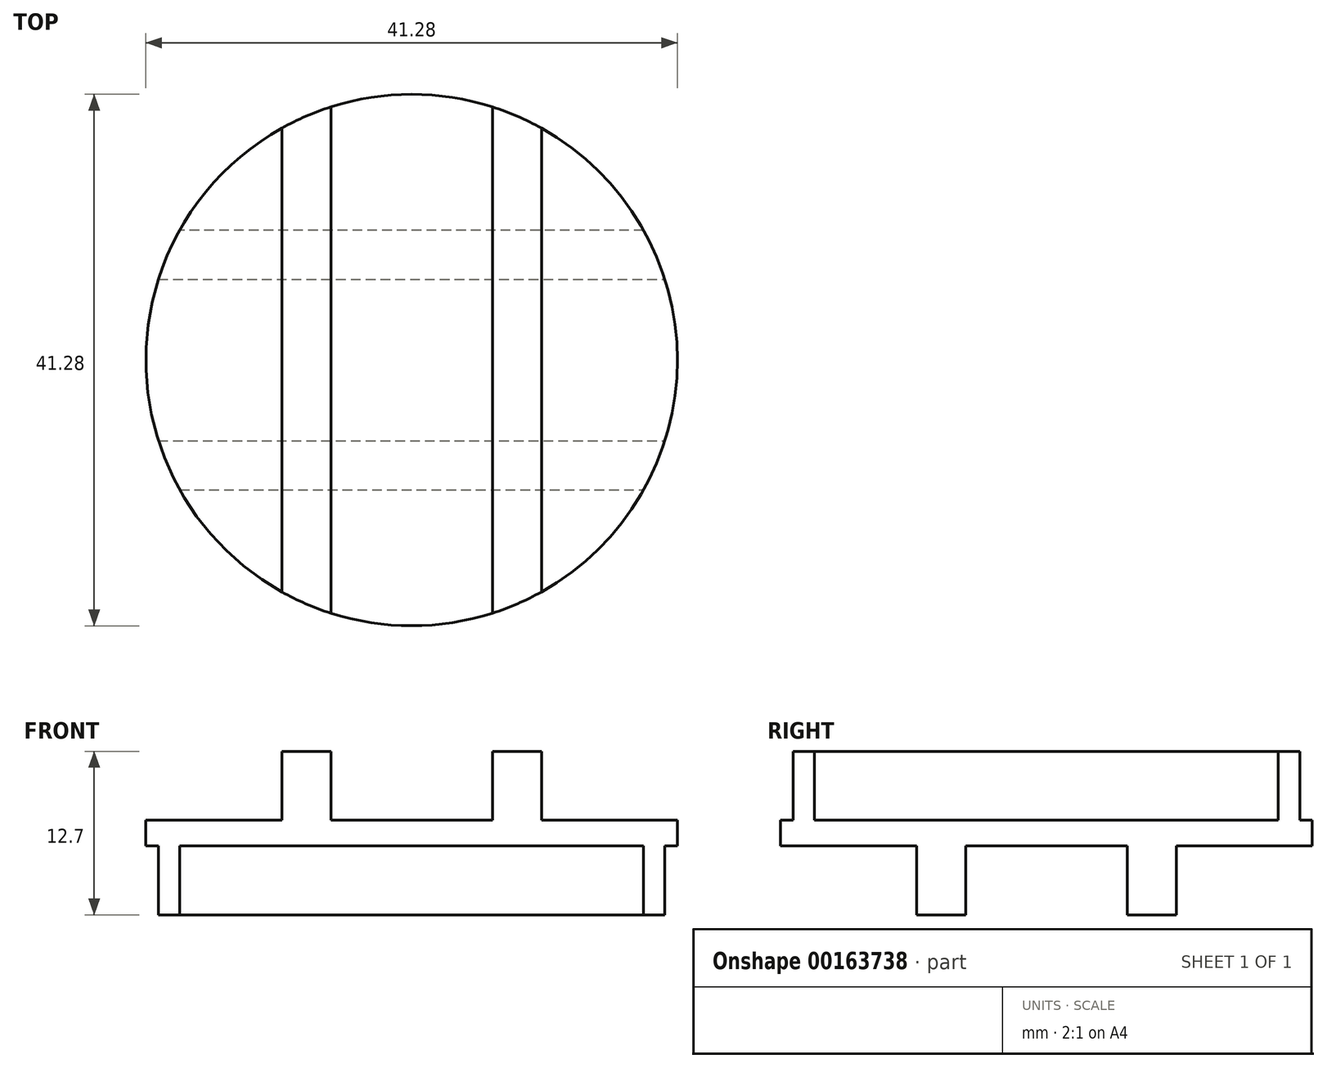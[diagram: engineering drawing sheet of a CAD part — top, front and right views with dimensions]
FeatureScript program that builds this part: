
annotation { "Feature Type Name" : "Feature", "Feature Type Description" : "" }
export const myFeature = defineFeature(function(context is Context, id is Id, definition is map)
    precondition{}
    {
        {
            var Q0;
            Q0=qCreatedBy(makeId("Top.planeOp"),FACE);
            var sketch = newSketch(context, id + "F0", { "sketchPlane" : qUnion([Q0])});
            skCircle(sketch, "E0", {"center": v(0, 0) * mm, "radius": 20.64 * mm});
            skSolve(sketch);
        }
        {
            var Q0;
            Q0=makeQuery(id+"F0.imprint","IMPRINT",FACE,{"disambiguationData":[TD([[makeQuery(id+"F0.imprint","IMPRINT",EDGE,{"derivedFrom":sQuery(id+"F0.wireOp",EDGE,"E0")}),1.0]])]});
            extrude(context, id + "F1", {"entities" : qUnion([Q0]), "depth" : 1 * mm, "hasSecondDirection" : true, "secondDirectionOppositeDirection" : true, "secondDirectionDepth" : 1 * mm});
        }
        {
            var Q0;
            Q0=makeQuery(id+"F1.opExtrude","CAP_FACE",FACE,{"disambiguationData":[OSD([sQuery(id+"F0.wireOp",EDGE,"E0")])],"isStart":false});
            var sketch = newSketch(context, id + "F2", { "sketchPlane" : qUnion([Q0])});
            skLineSegment(sketch, "E1", {"start": v(-10.08, -18) * mm, "end": v(-10.08, 18) * mm});
            skLineSegment(sketch, "E2", {"start": v(10.08, -18) * mm, "end": v(10.08, 18) * mm});
            skLineSegment(sketch, "E3", {"start": v(-10.08, 0) * mm, "end": v(10.08, 0) * mm, "construction": true});
            skLineSegment(sketch, "E4", {"start": v(-6.27, -19.66) * mm, "end": v(-6.27, 19.66) * mm});
            skLineSegment(sketch, "E5", {"start": v(6.27, -19.66) * mm, "end": v(6.27, 19.66) * mm});
            skLineSegment(sketch, "E6", {"start": v(-6.27, 0) * mm, "end": v(6.27, 0) * mm, "construction": true});
            skSolve(sketch);
        }
        {
            var Q0;
            {var subQ7=sQuery(id+"F2.wireOp",EDGE,"E1");Q0=makeQuery(id+"F2.imprint","IMPRINT",FACE,{"disambiguationData":[TD([[makeQuery(id+"F2.imprint","IMPRINT",EDGE,{"derivedFrom":subQ7}),-1.0]])]});}
            var Q1;
            {var subQ7=sQuery(id+"F2.wireOp",EDGE,"E2");Q1=makeQuery(id+"F2.imprint","IMPRINT",FACE,{"disambiguationData":[TD([[makeQuery(id+"F2.imprint","IMPRINT",EDGE,{"derivedFrom":subQ7}),1.0]])]});}
            extrude(context, id + "F3", {"entities" : qUnion([Q0, Q1]), "operationType" : NewBodyOperationType.ADD, "depth" : 6.35 * mm - 1 * mm});
        }
        {
            var Q0;
            Q0=makeQuery(id+"F1.opExtrude","CAP_FACE",FACE,{"disambiguationData":[OSD([sQuery(id+"F0.wireOp",EDGE,"E0")])],"isStart":true});
            var sketch = newSketch(context, id + "F4", { "sketchPlane" : qUnion([Q0])});
            skLineSegment(sketch, "E7", {"start": v(-18, 10.08) * mm, "end": v(18, 10.08) * mm});
            skLineSegment(sketch, "E8", {"start": v(-19.66, 6.27) * mm, "end": v(19.66, 6.27) * mm});
            skLineSegment(sketch, "E9", {"start": v(-19.66, -6.27) * mm, "end": v(19.66, -6.27) * mm});
            skLineSegment(sketch, "E10", {"start": v(18, -10.08) * mm, "end": v(-18, -10.08) * mm});
            skLineSegment(sketch, "E11", {"start": v(0, 10.08) * mm, "end": v(0, -10.08) * mm, "construction": true});
            skLineSegment(sketch, "E12", {"start": v(0, 6.27) * mm, "end": v(0, -6.27) * mm, "construction": true});
            skLineSegment(sketch, "E13", {"start": v(-9.3, 0) * mm, "end": v(9.17, 0) * mm, "construction": true});
            skSolve(sketch);
        }
        {
            var Q0;
            {var subQ7=sQuery(id+"F4.wireOp",EDGE,"E7");Q0=makeQuery(id+"F4.imprint","IMPRINT",FACE,{"disambiguationData":[TD([[makeQuery(id+"F4.imprint","IMPRINT",EDGE,{"derivedFrom":subQ7}),-1.0]])]});}
            var Q1;
            {var subQ0=sQuery(id+"F4.wireOp",EDGE,"E10");Q1=makeQuery(id+"F4.imprint","IMPRINT",FACE,{"disambiguationData":[TD([[makeQuery(id+"F4.imprint","IMPRINT",EDGE,{"derivedFrom":subQ0}),-1.0]])]});}
            extrude(context, id + "F5", {"entities" : qUnion([Q0, Q1]), "operationType" : NewBodyOperationType.ADD, "depth" : 6.35 * mm - 1 * mm});
        }
    });
